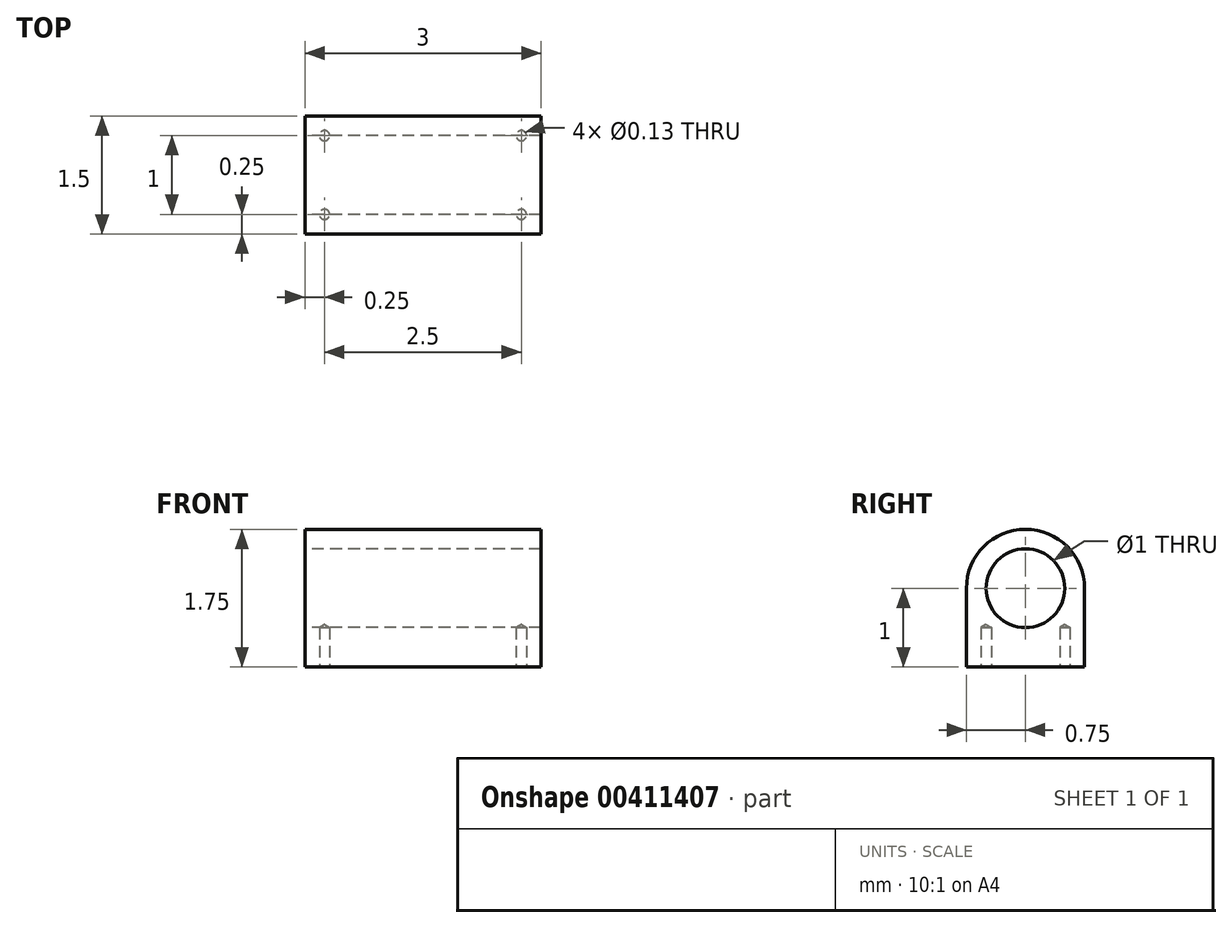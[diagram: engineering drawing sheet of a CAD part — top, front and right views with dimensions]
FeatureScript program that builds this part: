
annotation { "Feature Type Name" : "Feature", "Feature Type Description" : "" }
export const myFeature = defineFeature(function(context is Context, id is Id, definition is map)
    precondition{}
    {
        {
            var Q0;
            Q0=qCreatedBy(makeId("Right.planeOp"),FACE);
            var sketch = newSketch(context, id + "F0", { "sketchPlane" : qUnion([Q0])});
            skCircle(sketch, "E0", {"center": v(0, 0) * mm, "radius": 0.5 * mm});
            skArc(sketch, "E1", {"start": v(0.75, 0) * mm, "mid": v(0, 0.75) * mm, "end": v(-0.75, 0) * mm});
            skLineSegment(sketch, "E2", {"start": v(0.75, -1) * mm, "end": v(0.75, 0) * mm});
            skLineSegment(sketch, "E3", {"start": v(-0.75, -1) * mm, "end": v(-0.75, 0) * mm});
            skLineSegment(sketch, "E4", {"start": v(-0.75, -1) * mm, "end": v(0.75, -1) * mm});
            skSolve(sketch);
        }
        {
            var Q0;
            Q0=makeQuery(id+"F0.imprint","IMPRINT",FACE,{"disambiguationData":[TD([[makeQuery(id+"F0.imprint","IMPRINT",EDGE,{"derivedFrom":sQuery(id+"F0.wireOp",EDGE,"E0")}),-1.0]])]});
            extrude(context, id + "F1", {"entities" : qUnion([Q0]), "depth" : 3 * mm});
        }
        {
            var Q0;
            Q0=makeQuery(id+"F1.opExtrude","SWEPT_FACE",FACE,{"disambiguationData":[OSD([sQuery(id+"F0.wireOp",EDGE,"E4")])]});
            var sketch = newSketch(context, id + "F2", { "sketchPlane" : qUnion([Q0])});
            skLineSegment(sketch, "E5.0", {"start": v(0.25, 0.75) * mm, "end": v(0.25, -0.75) * mm, "construction": true});
            skLineSegment(sketch, "E6.0", {"start": v(2.75, 0.75) * mm, "end": v(2.75, -0.75) * mm, "construction": true});
            skLineSegment(sketch, "E7.0", {"start": v(3, 0.5) * mm, "end": v(0, 0.5) * mm, "construction": true});
            skLineSegment(sketch, "E8.0", {"start": v(3, -0.75) * mm, "end": v(0, -0.75) * mm});
            skLineSegment(sketch, "E9.0", {"start": v(3, -0.5) * mm, "end": v(0, -0.5) * mm, "construction": true});
            skLineSegment(sketch, "E10", {"start": v(-0.27, 0) * mm, "end": v(3.35, 0) * mm, "construction": true});
            skPoint(sketch, "E10.endSnap0", {"position": v(3, 0) * mm});
            skCircle(sketch, "E11", {"center": v(2.75, 0.5) * mm, "radius": 0.07 * mm});
            skCircle(sketch, "E12.MirrorC", {"center": v(2.75, -0.5) * mm, "radius": 0.07 * mm});
            skCircle(sketch, "E13", {"center": v(0.25, 0.5) * mm, "radius": 0.07 * mm});
            skCircle(sketch, "E14.MirrorC", {"center": v(0.25, -0.5) * mm, "radius": 0.07 * mm});
            skSolve(sketch);
        }
        {
            var Q0;
            Q0=sQuery(id+"F2.wireOp",VERTEX,"E13.center");
            var Q1;
            Q1=makeQuery(id+"F1.opExtrude","SWEPT_BODY",BODY,{"disambiguationData":[OSD([sQuery(id+"F0.wireOp",EDGE,"E0"),sQuery(id+"F0.wireOp",EDGE,"E1"),sQuery(id+"F0.wireOp",EDGE,"E2"),sQuery(id+"F0.wireOp",EDGE,"E3"),sQuery(id+"F0.wireOp",EDGE,"E4")])]});
            hole(context, id + "F3", {"style" : HoleStyle.SIMPLE, "endStyle" : HoleEndStyle.BLIND, "holeDiameter" : 0.13 * mm, "holeDepth" : 0.5 * mm, "isTappedThrough" : true, "tappedDepth" : 12 * mm, "tapClearance" : 3, "startFromSketch" : true, "locations" : qUnion([Q0]), "scope" : qUnion([Q1])});
        }
        {
            var Q0;
            Q0=sQuery(id+"F2.wireOp",VERTEX,"E11.center");
            var Q1;
            Q1=sQuery(id+"F2.wireOp",VERTEX,"E12.MirrorC.center");
            var Q2;
            Q2=sQuery(id+"F2.wireOp",VERTEX,"E14.MirrorC.center");
            var Q3;
            Q3=makeQuery(id+"F1.opExtrude","SWEPT_BODY",BODY,{"disambiguationData":[OSD([sQuery(id+"F0.wireOp",EDGE,"E0"),sQuery(id+"F0.wireOp",EDGE,"E1"),sQuery(id+"F0.wireOp",EDGE,"E2"),sQuery(id+"F0.wireOp",EDGE,"E3"),sQuery(id+"F0.wireOp",EDGE,"E4")])]});
            hole(context, id + "F4", {"style" : HoleStyle.SIMPLE, "endStyle" : HoleEndStyle.BLIND, "holeDiameter" : 0.13 * mm, "holeDepth" : 0.5 * mm, "isTappedThrough" : true, "tappedDepth" : 12 * mm, "tapClearance" : 3, "startFromSketch" : true, "locations" : qUnion([Q0, Q1, Q2]), "scope" : qUnion([Q3])});
        }
    });
